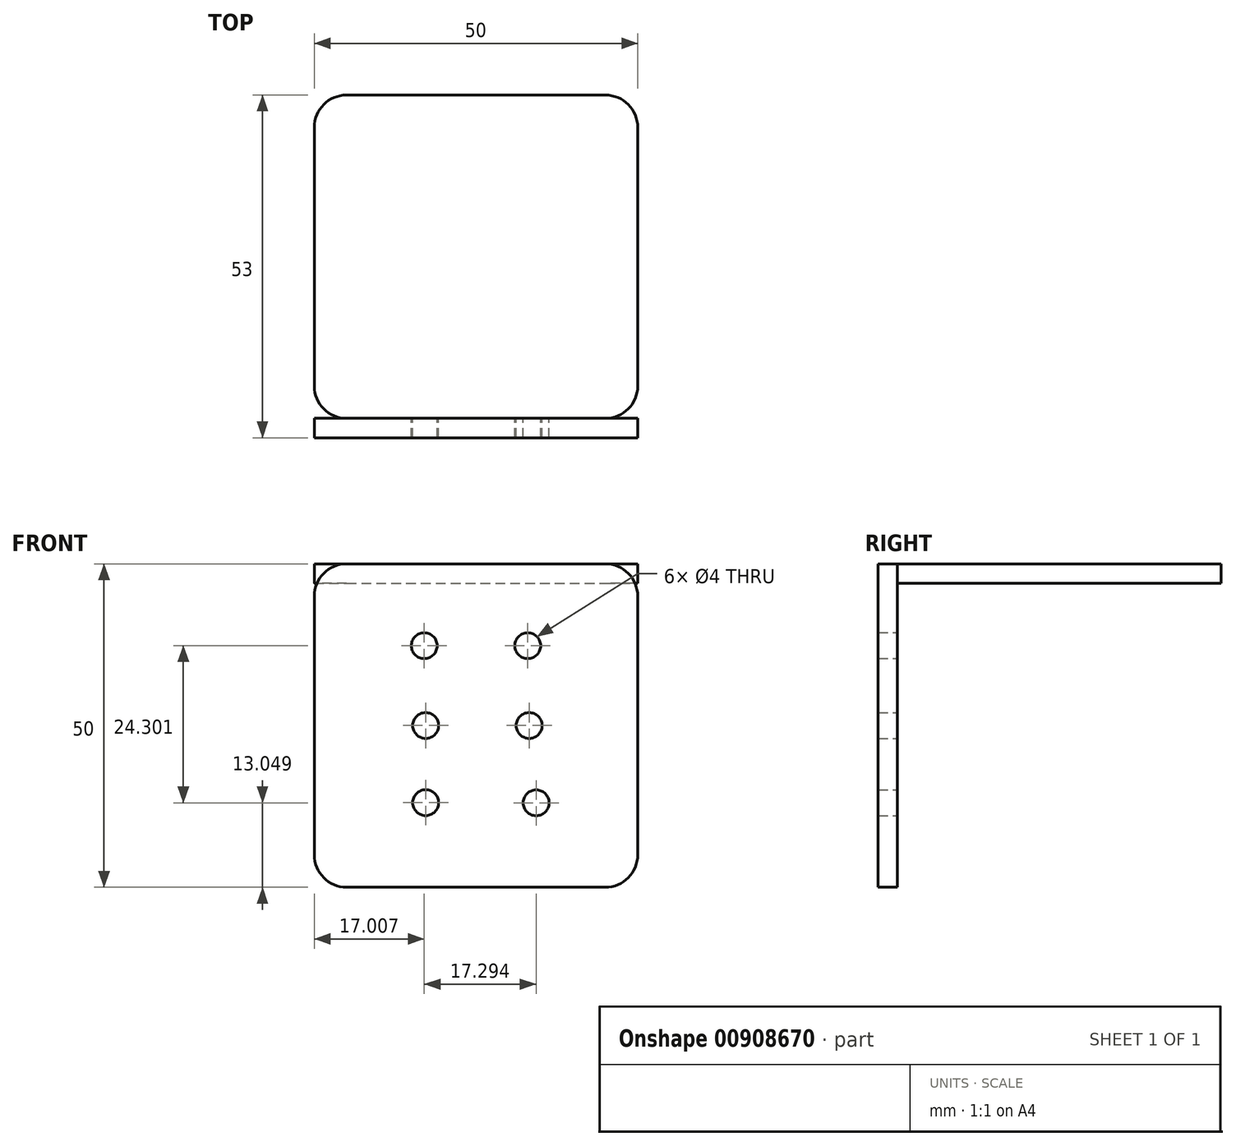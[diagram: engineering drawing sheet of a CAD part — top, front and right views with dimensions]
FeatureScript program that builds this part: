
annotation { "Feature Type Name" : "Feature", "Feature Type Description" : "" }
export const myFeature = defineFeature(function(context is Context, id is Id, definition is map)
    precondition{}
    {
        {
            var Q0;
            Q0=qCreatedBy(makeId("Front.planeOp"),FACE);
            var sketch = newSketch(context, id + "F0", { "sketchPlane" : qUnion([Q0])});
            skLineSegment(sketch, "E0.bottom", {"start": v(-25, -25) * mm, "end": v(25, -25) * mm});
            skLineSegment(sketch, "E0.top", {"start": v(-25, 25) * mm, "end": v(25, 25) * mm});
            skLineSegment(sketch, "E0.left", {"start": v(-25, -25) * mm, "end": v(-25, 25) * mm});
            skLineSegment(sketch, "E0.right", {"start": v(25, -25) * mm, "end": v(25, 25) * mm});
            skPoint(sketch, "E0.middle", {"position": v(0, 0) * mm});
            skCircle(sketch, "E1", {"center": v(-8, 12.35) * mm, "radius": 2 * mm});
            skCircle(sketch, "E2", {"center": v(8, 12.35) * mm, "radius": 2 * mm});
            skCircle(sketch, "E3", {"center": v(-7.78, 0) * mm, "radius": 2 * mm});
            skCircle(sketch, "E4", {"center": v(8.22, 0) * mm, "radius": 2 * mm});
            skCircle(sketch, "E5", {"center": v(-7.78, -11.93) * mm, "radius": 2 * mm});
            skCircle(sketch, "E6", {"center": v(9.3, -11.95) * mm, "radius": 2 * mm});
            skSolve(sketch);
        }
        {
            var Q0;
            Q0 = qSketchRegion(id + "F0", true);
            extrude(context, id + "F1", {"entities" : qUnion([Q0]), "endBound" : BoundingType.SYMMETRIC, "depth" : 3 * mm, "offsetDistance" : 25 * mm});
        }
        {
            var Q0;
            Q0=makeQuery(id+"F1.opExtrude","SWEPT_EDGE",EDGE,{"disambiguationData":[OSD([sQuery(id+"F0.wireOp",EDGE,"E0.top"),sQuery(id+"F0.wireOp",EDGE,"E0.left")])]});
            var Q1;
            Q1=makeQuery(id+"F1.opExtrude","SWEPT_EDGE",EDGE,{"disambiguationData":[OSD([sQuery(id+"F0.wireOp",EDGE,"E0.top"),sQuery(id+"F0.wireOp",EDGE,"E0.right")])]});
            var Q2;
            Q2=makeQuery(id+"F1.opExtrude","SWEPT_EDGE",EDGE,{"disambiguationData":[OSD([sQuery(id+"F0.wireOp",EDGE,"E0.bottom"),sQuery(id+"F0.wireOp",EDGE,"E0.right")])]});
            var Q3;
            Q3=makeQuery(id+"F1.opExtrude","SWEPT_EDGE",EDGE,{"disambiguationData":[OSD([sQuery(id+"F0.wireOp",EDGE,"E0.bottom"),sQuery(id+"F0.wireOp",EDGE,"E0.left")])]});
            fillet(context, id + "F2", {"entities" : qUnion([Q0, Q1, Q2, Q3]), "radius" : 5 * mm, "tangentPropagation" : true, "allowEdgeOverflow" : false});
        }
        {
            var Q0;
            Q0=makeQuery(id+"F1.opExtrude","CAP_FACE",FACE,{"disambiguationData":[OSD([sQuery(id+"F0.wireOp",EDGE,"E0.bottom"),sQuery(id+"F0.wireOp",EDGE,"E0.top"),sQuery(id+"F0.wireOp",EDGE,"E0.left"),sQuery(id+"F0.wireOp",EDGE,"E0.right"),sQuery(id+"F0.wireOp",EDGE,"E1"),sQuery(id+"F0.wireOp",EDGE,"E2"),sQuery(id+"F0.wireOp",EDGE,"E3"),sQuery(id+"F0.wireOp",EDGE,"E4"),sQuery(id+"F0.wireOp",EDGE,"E5"),sQuery(id+"F0.wireOp",EDGE,"E6")])],"isStart":true});
            var sketch = newSketch(context, id + "F3", { "sketchPlane" : qUnion([Q0])});
            skLineSegment(sketch, "E7.top", {"start": v(-25, 25) * mm, "end": v(25, 25) * mm});
            skLineSegment(sketch, "E8", {"start": v(0, 25) * mm, "end": v(0, 22) * mm, "construction": true});
            skLineSegment(sketch, "E9", {"start": v(0, 22) * mm, "end": v(-25, 22) * mm});
            skLineSegment(sketch, "E10", {"start": v(-25, 22) * mm, "end": v(-25, 25) * mm});
            skLineSegment(sketch, "E11", {"start": v(0, 22) * mm, "end": v(25, 22) * mm});
            skLineSegment(sketch, "E12", {"start": v(25, 22) * mm, "end": v(25, 25) * mm});
            skSolve(sketch);
        }
        {
            var Q0;
            Q0 = qSketchRegion(id + "F3", true);
            extrude(context, id + "F4", {"entities" : qUnion([Q0]), "depth" : 50 * mm, "offsetDistance" : 25 * mm});
        }
        {
            var Q0;
            Q0=makeQuery(id+"F4.opExtrude","CAP_EDGE",EDGE,{"disambiguationData":[OSD([sQuery(id+"F3.wireOp",EDGE,"E10")])],"isStart":true});
            var Q1;
            Q1=makeQuery(id+"F4.opExtrude","CAP_EDGE",EDGE,{"disambiguationData":[OSD([sQuery(id+"F3.wireOp",EDGE,"E12")])],"isStart":true});
            var Q2;
            Q2=makeQuery(id+"F4.opExtrude","CAP_EDGE",EDGE,{"disambiguationData":[OSD([sQuery(id+"F3.wireOp",EDGE,"E10")])],"isStart":false});
            var Q3;
            Q3=makeQuery(id+"F4.opExtrude","CAP_EDGE",EDGE,{"disambiguationData":[OSD([sQuery(id+"F3.wireOp",EDGE,"E12")])],"isStart":false});
            fillet(context, id + "F5", {"entities" : qUnion([Q0, Q1, Q2, Q3]), "radius" : 5 * mm, "tangentPropagation" : true, "allowEdgeOverflow" : false});
        }
        {
            var Q0;
            Q0=qCreatedBy(makeId("Top.planeOp"),FACE);
            var sketch = newSketch(context, id + "F6", { "sketchPlane" : qUnion([Q0])});
            skCircle(sketch, "E13", {"center": v(-8.23, 35.58) * mm, "radius": 2 * mm});
            skCircle(sketch, "E14", {"center": v(8.34, 35.25) * mm, "radius": 2 * mm});
            skCircle(sketch, "E15", {"center": v(8.34, 15.25) * mm, "radius": 2 * mm});
            skCircle(sketch, "E16", {"center": v(0, 25.25) * mm, "radius": 2 * mm});
            skCircle(sketch, "E17", {"center": v(-8.23, 15.25) * mm, "radius": 2 * mm});
            skSolve(sketch);
        }
        {
            var Q0;
            Q0 = qSketchRegion(id + "F6", true);
            var Q1;
            Q1=sQuery(id+"F6.wireOp",EDGE,"E13");
            extrude(context, id + "F7", {"entities" : qUnion([Q0]), "operationType" : NewBodyOperationType.REMOVE, "surfaceEntities" : qUnion([Q1]), "endBound" : BoundingType.SYMMETRIC, "oppositeDirection" : true, "depth" : 3 * mm, "offsetDistance" : 25 * mm});
        }
    });
